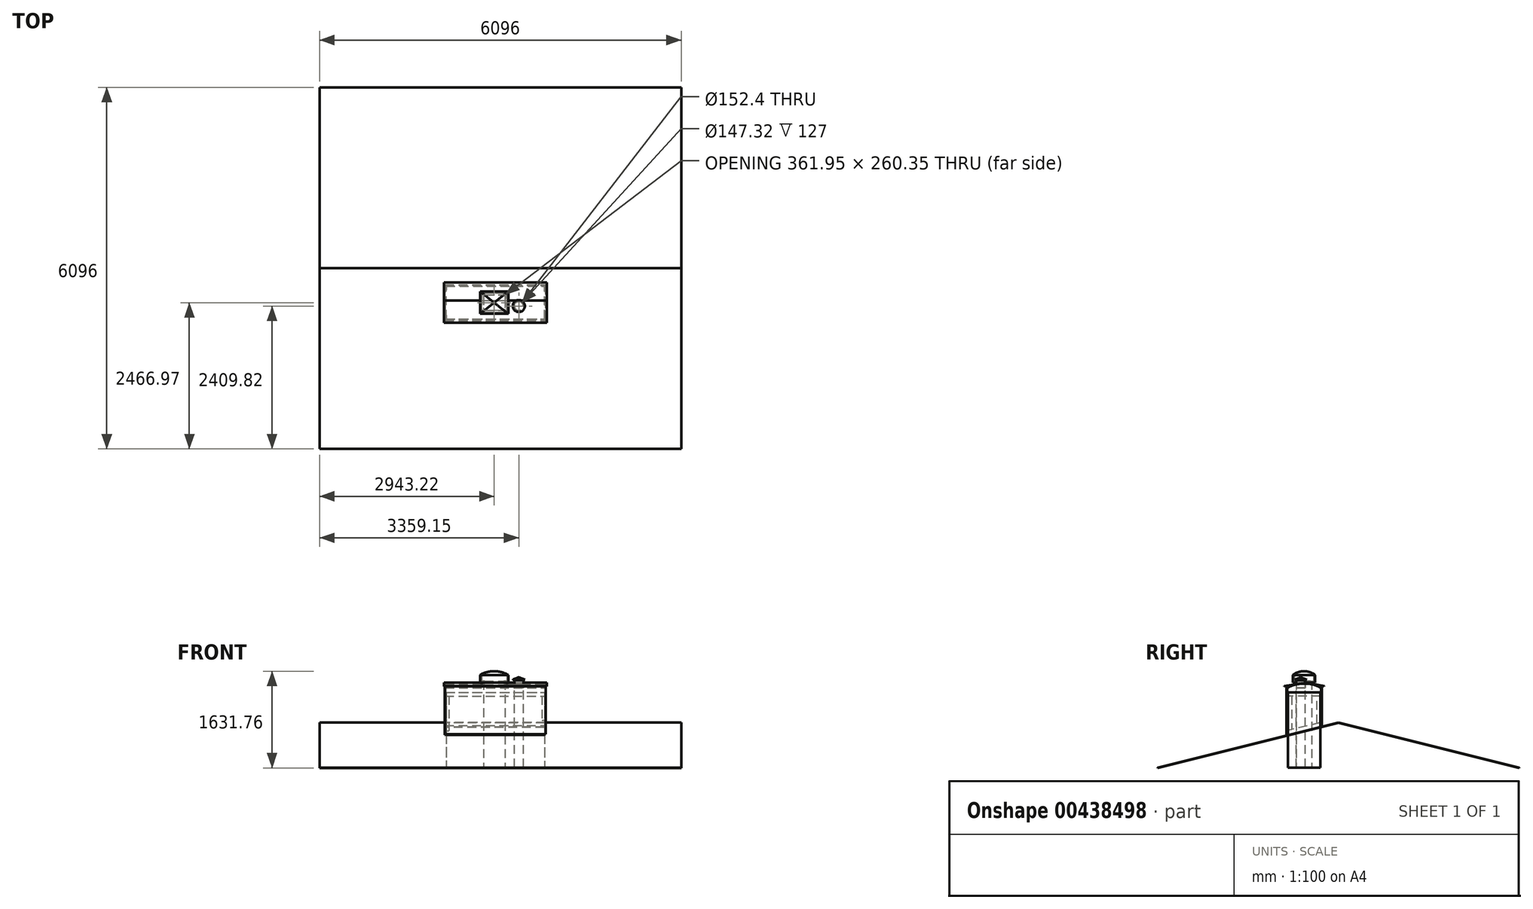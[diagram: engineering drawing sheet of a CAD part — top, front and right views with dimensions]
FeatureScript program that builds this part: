
annotation { "Feature Type Name" : "Feature", "Feature Type Description" : "" }
export const myFeature = defineFeature(function(context is Context, id is Id, definition is map)
    precondition{}
    {
        {
            var Q0;
            Q0=qCreatedBy(makeId("Right.planeOp"),FACE);
            var sketch = newSketch(context, id + "F0", { "sketchPlane" : qUnion([Q0])});
            skLineSegment(sketch, "E0", {"start": v(-3048, 0) * mm, "end": v(0, 762) * mm});
            skLineSegment(sketch, "E1", {"start": v(0, 762) * mm, "end": v(0, -40.65) * mm, "construction": true});
            skLineSegment(sketch, "E2.MirrorCS", {"start": v(3048, 0) * mm, "end": v(0, 762) * mm});
            skLineSegment(sketch, "E3.0", {"start": v(3046.46, -6.16) * mm, "end": v(0, 755.45) * mm});
            skLineSegment(sketch, "E3.1", {"start": v(-3046.46, -6.16) * mm, "end": v(0, 755.45) * mm});
            skLineSegment(sketch, "E4", {"start": v(-3048, 0) * mm, "end": v(-3046.46, -6.16) * mm});
            skLineSegment(sketch, "E5", {"start": v(3048, 0) * mm, "end": v(3046.46, -6.16) * mm});
            skSolve(sketch);
        }
        {
            var Q0;
            Q0=makeQuery(id+"F0.imprint","IMPRINT",FACE,{"disambiguationData":[TD([[makeQuery(id+"F0.imprint","IMPRINT",EDGE,{"derivedFrom":sQuery(id+"F0.wireOp",EDGE,"E0")}),-1.0]])]});
            var Q1;
            Q1=sQuery(id+"F0.wireOp",EDGE,"E0");
            var Q2;
            Q2=sQuery(id+"F0.wireOp",EDGE,"E2.MirrorCS");
            extrude(context, id + "F1", {"entities" : qUnion([Q0]), "surfaceEntities" : qUnion([Q1, Q2]), "depth" : 3048 * mm, "hasSecondDirection" : true, "secondDirectionOppositeDirection" : true, "secondDirectionDepth" : 3048 * mm, "offsetDistance" : 25.4 * mm});
        }
        {
            var Q0;
            Q0=qCreatedBy(makeId("Top.planeOp"),FACE);
            var sketch = newSketch(context, id + "F2", { "sketchPlane" : qUnion([Q0])});
            skLineSegment(sketch, "E6.bottom", {"start": v(-914.4, -854.07) * mm, "end": v(742.95, -854.07) * mm});
            skLineSegment(sketch, "E6.top", {"start": v(-914.4, -304.8) * mm, "end": v(742.95, -304.8) * mm});
            skLineSegment(sketch, "E6.left", {"start": v(-914.4, -854.07) * mm, "end": v(-914.4, -304.8) * mm});
            skLineSegment(sketch, "E6.right", {"start": v(742.95, -854.07) * mm, "end": v(742.95, -304.8) * mm});
            skSolve(sketch);
        }
        {
            var Q0;
            Q0=makeQuery(id+"F2.imprint","IMPRINT",FACE,{"disambiguationData":[TD([[makeQuery(id+"F2.imprint","IMPRINT",EDGE,{"derivedFrom":sQuery(id+"F2.wireOp",EDGE,"E6.bottom")}),1.0]])]});
            extrude(context, id + "F3", {"entities" : qUnion([Q0]), "operationType" : NewBodyOperationType.REMOVE, "endBound" : BoundingType.THROUGH_ALL, "depth" : 25.4 * mm, "offsetDistance" : 25.4 * mm});
        }
        {
            var Q0;
            Q0 = qSketchRegion(id + "F2", true);
            extrude(context, id + "F4", {"entities" : qUnion([Q0]), "depth" : 1270 * mm, "offsetDistance" : 25.4 * mm});
        }
        {
            var Q0;
            Q0=makeQuery(id+"F4.opExtrude","CAP_FACE",FACE,{"disambiguationData":[OSD([sQuery(id+"F2.wireOp",EDGE,"E6.bottom"),sQuery(id+"F2.wireOp",EDGE,"E6.top"),sQuery(id+"F2.wireOp",EDGE,"E6.left"),sQuery(id+"F2.wireOp",EDGE,"E6.right")])],"isStart":false});
            var sketch = newSketch(context, id + "F5", { "sketchPlane" : qUnion([Q0])});
            skLineSegment(sketch, "E7.bottom", {"start": v(-927.1, -866.77) * mm, "end": v(755.65, -866.77) * mm});
            skLineSegment(sketch, "E7.top", {"start": v(-927.1, -292.1) * mm, "end": v(755.65, -292.1) * mm});
            skLineSegment(sketch, "E7.left", {"start": v(-927.1, -866.77) * mm, "end": v(-927.1, -292.1) * mm});
            skLineSegment(sketch, "E7.right", {"start": v(755.65, -866.77) * mm, "end": v(755.65, -292.1) * mm});
            skSolve(sketch);
        }
        {
            var Q0;
            Q0 = qSketchRegion(id + "F5", true);
            extrude(context, id + "F6", {"entities" : qUnion([Q0]), "operationType" : NewBodyOperationType.ADD, "depth" : 76.2 * mm, "offsetDistance" : 25.4 * mm});
        }
        {
            var Q0;
            Q0=makeQuery(id+"F6.opExtrude","CAP_FACE",FACE,{"disambiguationData":[OSD([sQuery(id+"F5.wireOp",EDGE,"E7.bottom"),sQuery(id+"F5.wireOp",EDGE,"E7.top"),sQuery(id+"F5.wireOp",EDGE,"E7.left"),sQuery(id+"F5.wireOp",EDGE,"E7.right")])],"isStart":false});
            var sketch = newSketch(context, id + "F7", { "sketchPlane" : qUnion([Q0])});
            skLineSegment(sketch, "E8.bottom", {"start": v(-266.7, -419.1) * mm, "end": v(57.15, -419.1) * mm});
            skLineSegment(sketch, "E8.top", {"start": v(-266.7, -742.95) * mm, "end": v(57.15, -742.95) * mm});
            skLineSegment(sketch, "E8.left", {"start": v(-317.5, -469.9) * mm, "end": v(-317.5, -692.15) * mm});
            skLineSegment(sketch, "E8.right", {"start": v(107.95, -469.9) * mm, "end": v(107.95, -692.15) * mm});
            skPoint(sketch, "E9.visualSharp", {"position": v(-317.5, -419.1) * mm});
            skArc(sketch, "E9.filletArc", {"start": v(-266.7, -419.1) * mm, "mid": v(-302.62, -433.98) * mm, "end": v(-317.5, -469.9) * mm});
            skPoint(sketch, "E10.visualSharp", {"position": v(107.95, -419.1) * mm});
            skArc(sketch, "E10.filletArc", {"start": v(107.95, -469.9) * mm, "mid": v(93.07, -433.98) * mm, "end": v(57.15, -419.1) * mm});
            skPoint(sketch, "E11.visualSharp", {"position": v(107.95, -742.95) * mm});
            skArc(sketch, "E11.filletArc", {"start": v(57.15, -742.95) * mm, "mid": v(93.07, -728.07) * mm, "end": v(107.95, -692.15) * mm});
            skPoint(sketch, "E12.visualSharp", {"position": v(-317.5, -742.95) * mm});
            skArc(sketch, "E12.filletArc", {"start": v(-317.5, -692.15) * mm, "mid": v(-302.62, -728.07) * mm, "end": v(-266.7, -742.95) * mm});
            skCircle(sketch, "E13", {"center": v(311.15, -638.17) * mm, "radius": 76.2 * mm});
            skArc(sketch, "E14.0", {"start": v(-266.7, -450.85) * mm, "mid": v(-280.17, -456.43) * mm, "end": v(-285.75, -469.9) * mm});
            skLineSegment(sketch, "E14.1", {"start": v(-285.75, -469.9) * mm, "end": v(-285.75, -692.15) * mm});
            skLineSegment(sketch, "E14.2", {"start": v(-266.7, -450.85) * mm, "end": v(57.15, -450.85) * mm});
            skArc(sketch, "E14.3", {"start": v(-285.75, -692.15) * mm, "mid": v(-280.17, -705.62) * mm, "end": v(-266.7, -711.2) * mm});
            skArc(sketch, "E14.4", {"start": v(76.2, -469.9) * mm, "mid": v(70.62, -456.43) * mm, "end": v(57.15, -450.85) * mm});
            skLineSegment(sketch, "E14.5", {"start": v(76.2, -469.9) * mm, "end": v(76.2, -692.15) * mm});
            skArc(sketch, "E14.6", {"start": v(57.15, -711.2) * mm, "mid": v(70.62, -705.62) * mm, "end": v(76.2, -692.15) * mm});
            skLineSegment(sketch, "E14.7", {"start": v(-266.7, -711.2) * mm, "end": v(57.15, -711.2) * mm});
            skLineSegment(sketch, "E15.0", {"start": v(749.3, -298.45) * mm, "end": v(-920.75, -298.45) * mm});
            skLineSegment(sketch, "E15.1", {"start": v(749.3, -860.42) * mm, "end": v(749.3, -298.45) * mm});
            skLineSegment(sketch, "E15.2", {"start": v(-920.75, -860.42) * mm, "end": v(749.3, -860.42) * mm});
            skLineSegment(sketch, "E15.3", {"start": v(-920.75, -298.45) * mm, "end": v(-920.75, -860.42) * mm});
            skCircle(sketch, "E16.0", {"center": v(311.15, -638.17) * mm, "radius": 73.66 * mm});
            skSolve(sketch);
        }
        {
            var Q0;
            Q0=makeQuery(id+"F7.imprint","IMPRINT",FACE,{"disambiguationData":[TD([[makeQuery(id+"F7.imprint","IMPRINT",EDGE,{"derivedFrom":sQuery(id+"F7.wireOp",EDGE,"E8.bottom")}),-1.0]])]});
            extrude(context, id + "F8", {"entities" : qUnion([Q0]), "operationType" : NewBodyOperationType.ADD, "depth" : 114.3 * mm, "offsetDistance" : 25.4 * mm});
        }
        {
            var Q0;
            Q0=makeQuery(id+"F7.imprint","IMPRINT",FACE,{"disambiguationData":[TD([[makeQuery(id+"F7.imprint","IMPRINT",EDGE,{"derivedFrom":sQuery(id+"F7.wireOp",EDGE,"E13")}),1.0]])]});
            var Q1;
            Q1=makeQuery(id+"F7.imprint","IMPRINT",FACE,{"disambiguationData":[TD([[makeQuery(id+"F7.imprint","IMPRINT",EDGE,{"derivedFrom":sQuery(id+"F7.wireOp",EDGE,"E16.0")}),1.0]])]});
            extrude(context, id + "F9", {"entities" : qUnion([Q0, Q1]), "operationType" : NewBodyOperationType.REMOVE, "endBound" : BoundingType.THROUGH_ALL, "oppositeDirection" : true, "depth" : 25.4 * mm, "offsetDistance" : 25.4 * mm, "hasSecondDirection" : true, "secondDirectionBound" : SecondDirectionBoundingType.THROUGH_ALL, "secondDirectionOppositeDirection" : false, "secondDirectionDepth" : 25.4 * mm});
        }
        {
            var Q0;
            Q0=makeQuery(id+"F6.opExtrude","SWEPT_FACE",FACE,{"disambiguationData":[OSD([sQuery(id+"F5.wireOp",EDGE,"E7.right")])]});
            var sketch = newSketch(context, id + "F10", { "sketchPlane" : qUnion([Q0])});
            skArc(sketch, "E17", {"start": v(-292.1, 1346.2) * mm, "mid": v(-579.44, 1416.05) * mm, "end": v(-866.77, 1346.2) * mm});
            skLineSegment(sketch, "E18", {"start": v(-866.77, 1346.2) * mm, "end": v(-292.1, 1346.2) * mm});
            skSolve(sketch);
        }
        {
            var Q0;
            Q0=makeQuery(id+"F10.imprint","IMPRINT",FACE,{"disambiguationData":[TD([[makeQuery(id+"F10.imprint","IMPRINT",EDGE,{"derivedFrom":sQuery(id+"F10.wireOp",EDGE,"E17")}),1.0]])]});
            var Q1;
            Q1=makeQuery(id+"F6.opExtrude","SWEPT_FACE",FACE,{"disambiguationData":[OSD([sQuery(id+"F5.wireOp",EDGE,"E7.left")])]});
            extrude(context, id + "F11", {"entities" : qUnion([Q0]), "operationType" : NewBodyOperationType.ADD, "endBound" : BoundingType.UP_TO_SURFACE, "oppositeDirection" : true, "depth" : 25.4 * mm, "endBoundEntityFace" : qUnion([Q1]), "offsetDistance" : 25.4 * mm});
        }
        {
            var Q0;
            Q0=makeQuery(id+"F7.imprint","IMPRINT",FACE,{"disambiguationData":[TD([[makeQuery(id+"F7.imprint","IMPRINT",EDGE,{"derivedFrom":sQuery(id+"F7.wireOp",EDGE,"E13")}),1.0]])]});
            var Q1;
            Q1=makeQuery(id+"F7.imprint","IMPRINT",FACE,{"disambiguationData":[TD([[makeQuery(id+"F7.imprint","IMPRINT",EDGE,{"derivedFrom":sQuery(id+"F7.wireOp",EDGE,"E16.0")}),1.0]])]});
            extrude(context, id + "F12", {"entities" : qUnion([Q0, Q1]), "operationType" : NewBodyOperationType.REMOVE, "endBound" : BoundingType.THROUGH_ALL, "depth" : 25.4 * mm, "offsetDistance" : 25.4 * mm});
        }
        {
            var Q0;
            Q0=makeQuery(id+"F8.opExtrude","CAP_FACE",FACE,{"disambiguationData":[OSD([sQuery(id+"F7.wireOp",EDGE,"E8.bottom"),sQuery(id+"F7.wireOp",EDGE,"E8.top"),sQuery(id+"F7.wireOp",EDGE,"E8.left"),sQuery(id+"F7.wireOp",EDGE,"E8.right"),sQuery(id+"F7.wireOp",EDGE,"E9.filletArc"),sQuery(id+"F7.wireOp",EDGE,"E10.filletArc"),sQuery(id+"F7.wireOp",EDGE,"E11.filletArc"),sQuery(id+"F7.wireOp",EDGE,"E12.filletArc"),sQuery(id+"F7.wireOp",EDGE,"E14.0"),sQuery(id+"F7.wireOp",EDGE,"E14.1"),sQuery(id+"F7.wireOp",EDGE,"E14.2"),sQuery(id+"F7.wireOp",EDGE,"E14.3"),sQuery(id+"F7.wireOp",EDGE,"E14.4"),sQuery(id+"F7.wireOp",EDGE,"E14.5"),sQuery(id+"F7.wireOp",EDGE,"E14.6"),sQuery(id+"F7.wireOp",EDGE,"E14.7")])],"isStart":false});
            var sketch = newSketch(context, id + "F13", { "sketchPlane" : qUnion([Q0])});
            skLineSegment(sketch, "E19.0", {"start": v(-266.7, -450.85) * mm, "end": v(57.15, -450.85) * mm});
            skArc(sketch, "E20.0", {"start": v(76.2, -469.9) * mm, "mid": v(70.62, -456.43) * mm, "end": v(57.15, -450.85) * mm});
            skLineSegment(sketch, "E21.0", {"start": v(76.2, -469.9) * mm, "end": v(76.2, -692.15) * mm});
            skArc(sketch, "E22.0", {"start": v(57.15, -711.2) * mm, "mid": v(70.62, -705.62) * mm, "end": v(76.2, -692.15) * mm});
            skLineSegment(sketch, "E23.0", {"start": v(-266.7, -711.2) * mm, "end": v(57.15, -711.2) * mm});
            skArc(sketch, "E24.0", {"start": v(-285.75, -692.15) * mm, "mid": v(-280.17, -705.62) * mm, "end": v(-266.7, -711.2) * mm});
            skLineSegment(sketch, "E25.0", {"start": v(-285.75, -469.9) * mm, "end": v(-285.75, -692.15) * mm});
            skArc(sketch, "E26.0", {"start": v(-266.7, -450.85) * mm, "mid": v(-280.17, -456.43) * mm, "end": v(-285.75, -469.9) * mm});
            skSolve(sketch);
        }
        {
            var Q0;
            Q0=makeQuery(id+"F13.imprint","IMPRINT",FACE,{"disambiguationData":[TD([[makeQuery(id+"F13.imprint","IMPRINT",EDGE,{"derivedFrom":sQuery(id+"F13.wireOp",EDGE,"E19.0")}),-1.0]])]});
            extrude(context, id + "F14", {"entities" : qUnion([Q0]), "operationType" : NewBodyOperationType.REMOVE, "endBound" : BoundingType.THROUGH_ALL, "oppositeDirection" : true, "depth" : 25.4 * mm, "offsetDistance" : 25.4 * mm});
        }
        {
            var Q0;
            Q0=makeQuery(id+"F8.opExtrude","CAP_FACE",FACE,{"disambiguationData":[OSD([sQuery(id+"F7.wireOp",EDGE,"E8.bottom"),sQuery(id+"F7.wireOp",EDGE,"E8.top"),sQuery(id+"F7.wireOp",EDGE,"E8.left"),sQuery(id+"F7.wireOp",EDGE,"E8.right"),sQuery(id+"F7.wireOp",EDGE,"E9.filletArc"),sQuery(id+"F7.wireOp",EDGE,"E10.filletArc"),sQuery(id+"F7.wireOp",EDGE,"E11.filletArc"),sQuery(id+"F7.wireOp",EDGE,"E12.filletArc"),sQuery(id+"F7.wireOp",EDGE,"E14.0"),sQuery(id+"F7.wireOp",EDGE,"E14.1"),sQuery(id+"F7.wireOp",EDGE,"E14.2"),sQuery(id+"F7.wireOp",EDGE,"E14.3"),sQuery(id+"F7.wireOp",EDGE,"E14.4"),sQuery(id+"F7.wireOp",EDGE,"E14.5"),sQuery(id+"F7.wireOp",EDGE,"E14.6"),sQuery(id+"F7.wireOp",EDGE,"E14.7")])],"isStart":false});
            var sketch = newSketch(context, id + "F15", { "sketchPlane" : qUnion([Q0])});
            skLineSegment(sketch, "E27.bottom", {"start": v(-342.9, -768.35) * mm, "end": v(133.35, -768.35) * mm});
            skLineSegment(sketch, "E27.top", {"start": v(-342.9, -393.7) * mm, "end": v(133.35, -393.7) * mm});
            skLineSegment(sketch, "E27.left", {"start": v(-342.9, -768.35) * mm, "end": v(-342.9, -393.7) * mm});
            skLineSegment(sketch, "E27.right", {"start": v(133.35, -768.35) * mm, "end": v(133.35, -393.7) * mm});
            skLineSegment(sketch, "E28.0", {"start": v(-317.5, -742.95) * mm, "end": v(-317.5, -419.1) * mm});
            skLineSegment(sketch, "E28.1", {"start": v(-317.5, -742.95) * mm, "end": v(107.95, -742.95) * mm});
            skLineSegment(sketch, "E28.2", {"start": v(107.95, -742.95) * mm, "end": v(107.95, -419.1) * mm});
            skLineSegment(sketch, "E28.3", {"start": v(-317.5, -419.1) * mm, "end": v(107.95, -419.1) * mm});
            skSolve(sketch);
        }
        {
            var Q0;
            Q0=makeQuery(id+"F15.imprint","IMPRINT",FACE,{"disambiguationData":[TD([[makeQuery(id+"F15.imprint","IMPRINT",EDGE,{"derivedFrom":sQuery(id+"F15.wireOp",EDGE,"E27.bottom")}),1.0]])]});
            extrude(context, id + "F16", {"entities" : qUnion([Q0]), "depth" : 101.6 * mm, "offsetDistance" : 25.4 * mm, "hasSecondDirection" : true, "secondDirectionOppositeDirection" : true, "secondDirectionDepth" : 25.4 * mm});
        }
        {
            var Q0;
            Q0=makeQuery(id+"F16.opExtrude","SWEPT_FACE",FACE,{"disambiguationData":[OSD([sQuery(id+"F15.wireOp",EDGE,"E27.bottom")])]});
            var sketch = newSketch(context, id + "F17", { "sketchPlane" : qUnion([Q0])});
            skArc(sketch, "E29", {"start": v(133.35, 1562.1) * mm, "mid": v(-104.77, 1625.6) * mm, "end": v(-342.9, 1562.1) * mm});
            skSolve(sketch);
        }
        {
            var Q0;
            Q0=makeQuery(id+"F16.opExtrude","SWEPT_FACE",FACE,{"disambiguationData":[OSD([sQuery(id+"F15.wireOp",EDGE,"E27.right")])]});
            var sketch = newSketch(context, id + "F18", { "sketchPlane" : qUnion([Q0])});
            skArc(sketch, "E30", {"start": v(-393.7, 1562.1) * mm, "mid": v(-581.02, 1625.6) * mm, "end": v(-768.35, 1562.1) * mm});
            skLineSegment(sketch, "E31.top", {"start": v(-768.35, 1738.66) * mm, "end": v(-393.7, 1738.66) * mm});
            skLineSegment(sketch, "E31.left", {"start": v(-768.35, 1562.1) * mm, "end": v(-768.35, 1738.66) * mm});
            skLineSegment(sketch, "E31.right", {"start": v(-393.7, 1562.1) * mm, "end": v(-393.7, 1738.66) * mm});
            skSolve(sketch);
        }
        {
            var Q0;
            Q0=makeQuery(id+"F17.imprint","IMPRINT",FACE,{"disambiguationData":[TD([[makeQuery(id+"F17.imprint","IMPRINT",EDGE,{"derivedFrom":sQuery(id+"F17.wireOp",EDGE,"E29")}),1.0]])]});
            var Q1;
            Q1=makeQuery(id+"F16.opExtrude","SWEPT_FACE",FACE,{"disambiguationData":[OSD([sQuery(id+"F15.wireOp",EDGE,"E27.top")])]});
            extrude(context, id + "F19", {"entities" : qUnion([Q0]), "operationType" : NewBodyOperationType.ADD, "endBound" : BoundingType.UP_TO_SURFACE, "oppositeDirection" : true, "depth" : 25.4 * mm, "endBoundEntityFace" : qUnion([Q1]), "offsetDistance" : 25.4 * mm});
        }
        {
            var Q0;
            Q0=makeQuery(id+"F18.imprint","IMPRINT",FACE,{"disambiguationData":[TD([[makeQuery(id+"F18.imprint","IMPRINT",EDGE,{"derivedFrom":sQuery(id+"F18.wireOp",EDGE,"E30")}),-1.0]])]});
            extrude(context, id + "F20", {"entities" : qUnion([Q0]), "operationType" : NewBodyOperationType.REMOVE, "endBound" : BoundingType.THROUGH_ALL, "oppositeDirection" : true, "depth" : 25.4 * mm, "offsetDistance" : 25.4 * mm});
        }
        {
            var Q0;
            Q0=makeQuery(id+"F7.imprint","IMPRINT",FACE,{"disambiguationData":[TD([[makeQuery(id+"F7.imprint","IMPRINT",EDGE,{"derivedFrom":sQuery(id+"F7.wireOp",EDGE,"E13")}),1.0]])]});
            extrude(context, id + "F21", {"entities" : qUnion([Q0]), "depth" : 127 * mm, "offsetDistance" : 25.4 * mm});
        }
        {
            var Q0;
            Q0=makeQuery(id+"F21.opExtrude","SWEPT_FACE",FACE,{"disambiguationData":[OSD([sQuery(id+"F7.wireOp",EDGE,"E13")])]});
            cPlane(context, id + "F22", {"entities" : qUnion([Q0]), "cplaneType" : CPlaneType.LINE_ANGLE, "offset" : 25.4 * mm, "angle" : 0 * degree, "width" : 152.4 * mm, "height" : 152.4 * mm});
        }
        {
            var Q0;
            Q0=qCreatedBy(id+"F22.planeOp",FACE);
            var sketch = newSketch(context, id + "F23", { "sketchPlane" : qUnion([Q0])});
            skLineSegment(sketch, "E32", {"start": v(638.17, 1430.23) * mm, "end": v(638.17, 1564.53) * mm, "construction": true});
            skLineSegment(sketch, "E33", {"start": v(638.17, 1521.29) * mm, "end": v(537.47, 1483.52) * mm});
            skLineSegment(sketch, "E34", {"start": v(537.47, 1483.52) * mm, "end": v(536.57, 1485.9) * mm});
            skLineSegment(sketch, "E35", {"start": v(536.57, 1485.9) * mm, "end": v(638.17, 1524) * mm});
            skLineSegment(sketch, "E36", {"start": v(638.17, 1524) * mm, "end": v(638.17, 1521.29) * mm});
            skSolve(sketch);
        }
        {
            var Q0;
            Q0=makeQuery(id+"F23.imprint","IMPRINT",FACE,{"disambiguationData":[TD([[makeQuery(id+"F23.imprint","IMPRINT",EDGE,{"derivedFrom":sQuery(id+"F23.wireOp",EDGE,"E33")}),-1.0]])]});
            var Q1;
            Q1=sQuery(id+"F23.wireOp",EDGE,"E32");
            revolve(context, id + "F24", {"operationType" : NewBodyOperationType.ADD, "entities" : qUnion([Q0]), "axis" : qUnion([Q1]), "revolveType" : RevolveType.FULL});
        }
        {
            var Q0;
            Q0=makeQuery(id+"F4.opExtrude","SWEPT_FACE",FACE,{"disambiguationData":[OSD([sQuery(id+"F2.wireOp",EDGE,"E6.bottom")])]});
            var sketch = newSketch(context, id + "F25", { "sketchPlane" : qUnion([Q0])});
            skLineSegment(sketch, "E37.bottom", {"start": v(-933.45, 1270) * mm, "end": v(762, 1270) * mm});
            skLineSegment(sketch, "E37.top", {"start": v(-933.45, 1206.5) * mm, "end": v(762, 1206.5) * mm});
            skLineSegment(sketch, "E37.left", {"start": v(-933.45, 1270) * mm, "end": v(-933.45, 1206.5) * mm});
            skLineSegment(sketch, "E37.right", {"start": v(762, 1270) * mm, "end": v(762, 1206.5) * mm});
            skLineSegment(sketch, "E38.bottom", {"start": v(-933.45, 622.3) * mm, "end": v(762, 622.3) * mm});
            skLineSegment(sketch, "E38.top", {"start": v(-933.45, 558.8) * mm, "end": v(762, 558.8) * mm});
            skLineSegment(sketch, "E38.left", {"start": v(-933.45, 622.3) * mm, "end": v(-933.45, 558.8) * mm});
            skLineSegment(sketch, "E38.right", {"start": v(762, 622.3) * mm, "end": v(762, 558.8) * mm});
            skLineSegment(sketch, "E39.bottom", {"start": v(-933.45, 1206.5) * mm, "end": v(-869.95, 1206.5) * mm});
            skLineSegment(sketch, "E39.top", {"start": v(-933.45, 622.3) * mm, "end": v(-869.95, 622.3) * mm});
            skLineSegment(sketch, "E39.left", {"start": v(-933.45, 1206.5) * mm, "end": v(-933.45, 622.3) * mm});
            skLineSegment(sketch, "E39.right", {"start": v(-869.95, 1206.5) * mm, "end": v(-869.95, 622.3) * mm});
            skLineSegment(sketch, "E40.bottom", {"start": v(762, 1206.5) * mm, "end": v(698.5, 1206.5) * mm});
            skLineSegment(sketch, "E40.top", {"start": v(762, 622.3) * mm, "end": v(698.5, 622.3) * mm});
            skLineSegment(sketch, "E40.left", {"start": v(762, 1206.5) * mm, "end": v(762, 622.3) * mm});
            skLineSegment(sketch, "E40.right", {"start": v(698.5, 1206.5) * mm, "end": v(698.5, 622.3) * mm});
            skSolve(sketch);
        }
        {
            var Q0;
            {var subQ1=sQuery(id+"F25.wireOp",EDGE,"E37.top");Q0=makeQuery(id+"F25.imprint","IMPRINT",FACE,{"disambiguationData":[TD([[makeQuery(id+"F25.imprint","IMPRINT",EDGE,{"derivedFrom":subQ1}),1.0]])]});}
            var Q1;
            {var subQ3=sQuery(id+"F25.wireOp",EDGE,"E37.left");Q1=makeQuery(id+"F25.imprint","IMPRINT",FACE,{"disambiguationData":[TD([[makeQuery(id+"F25.imprint","IMPRINT",EDGE,{"derivedFrom":subQ3}),1.0]])]});}
            var Q2;
            {var subQ3=sQuery(id+"F25.wireOp",EDGE,"E37.right");Q2=makeQuery(id+"F25.imprint","IMPRINT",FACE,{"disambiguationData":[TD([[makeQuery(id+"F25.imprint","IMPRINT",EDGE,{"derivedFrom":subQ3}),-1.0]])]});}
            extrude(context, id + "F26", {"entities" : qUnion([Q0, Q1, Q2]), "depth" : 19.05 * mm, "offsetDistance" : 25.4 * mm});
        }
        {
            var Q0;
            {var subQ0=sQuery(id+"F25.wireOp",EDGE,"E39.right");Q0=makeQuery(id+"F25.imprint","IMPRINT",FACE,{"disambiguationData":[TD([[makeQuery(id+"F25.imprint","IMPRINT",EDGE,{"derivedFrom":subQ0}),-1.0]])]});}
            var Q1;
            {var subQ0=sQuery(id+"F25.wireOp",EDGE,"E39.left");Q1=makeQuery(id+"F25.imprint","IMPRINT",FACE,{"disambiguationData":[TD([[makeQuery(id+"F25.imprint","IMPRINT",EDGE,{"derivedFrom":subQ0}),1.0]])]});}
            extrude(context, id + "F27", {"entities" : qUnion([Q0, Q1]), "depth" : 19.05 * mm, "offsetDistance" : 25.4 * mm});
        }
        {
            var Q0;
            Q0=makeQuery(id+"F4.opExtrude","SWEPT_FACE",FACE,{"disambiguationData":[OSD([sQuery(id+"F2.wireOp",EDGE,"E6.left")])]});
            var sketch = newSketch(context, id + "F28", { "sketchPlane" : qUnion([Q0])});
            skLineSegment(sketch, "E41.bottom", {"start": v(301.62, 1270) * mm, "end": v(854.07, 1270) * mm});
            skLineSegment(sketch, "E41.top", {"start": v(301.62, 1206.5) * mm, "end": v(854.07, 1206.5) * mm});
            skLineSegment(sketch, "E41.left", {"start": v(301.62, 1270) * mm, "end": v(301.62, 1206.5) * mm});
            skLineSegment(sketch, "E41.right", {"start": v(854.07, 1270) * mm, "end": v(854.07, 1206.5) * mm});
            skLineSegment(sketch, "E42", {"start": v(854.07, 558.8) * mm, "end": v(301.62, 693.33) * mm});
            skLineSegment(sketch, "E43", {"start": v(301.62, 693.33) * mm, "end": v(301.62, 758.69) * mm});
            skLineSegment(sketch, "E44", {"start": v(301.62, 758.69) * mm, "end": v(854.07, 624.16) * mm});
            skLineSegment(sketch, "E45", {"start": v(854.07, 624.16) * mm, "end": v(854.07, 558.8) * mm});
            skLineSegment(sketch, "E46", {"start": v(301.62, 1206.5) * mm, "end": v(301.62, 758.69) * mm});
            skLineSegment(sketch, "E47", {"start": v(365.12, 743.22) * mm, "end": v(365.12, 1206.5) * mm});
            skLineSegment(sketch, "E48", {"start": v(854.07, 1206.5) * mm, "end": v(854.07, 624.16) * mm});
            skLineSegment(sketch, "E49", {"start": v(790.57, 1206.5) * mm, "end": v(790.57, 639.62) * mm});
            skSolve(sketch);
        }
        {
            var Q0;
            {var subQ5=sQuery(id+"F28.wireOp",EDGE,"E41.right");Q0=makeQuery(id+"F28.imprint","IMPRINT",FACE,{"disambiguationData":[TD([[makeQuery(id+"F28.imprint","IMPRINT",EDGE,{"derivedFrom":subQ5}),-1.0]])]});}
            var Q1;
            {var subQ3=sQuery(id+"F28.wireOp",EDGE,"E41.left");Q1=makeQuery(id+"F28.imprint","IMPRINT",FACE,{"disambiguationData":[TD([[makeQuery(id+"F28.imprint","IMPRINT",EDGE,{"derivedFrom":subQ3}),1.0]])]});}
            extrude(context, id + "F29", {"entities" : qUnion([Q0, Q1]), "depth" : 19.05 * mm, "offsetDistance" : 25.4 * mm});
        }
        {
            var Q0;
            {var subQ0=sQuery(id+"F28.wireOp",EDGE,"E47");Q0=makeQuery(id+"F28.imprint","IMPRINT",FACE,{"disambiguationData":[TD([[makeQuery(id+"F28.imprint","IMPRINT",EDGE,{"derivedFrom":subQ0}),1.0]])]});}
            var Q1;
            {var subQ0=sQuery(id+"F28.wireOp",EDGE,"E46");Q1=makeQuery(id+"F28.imprint","IMPRINT",FACE,{"disambiguationData":[TD([[makeQuery(id+"F28.imprint","IMPRINT",EDGE,{"derivedFrom":subQ0}),1.0]])]});}
            extrude(context, id + "F30", {"entities" : qUnion([Q0, Q1]), "depth" : 19.05 * mm, "offsetDistance" : 25.4 * mm});
        }
        {
            var Q0;
            {var subQ0=sQuery(id+"F28.wireOp",EDGE,"E48");Q0=makeQuery(id+"F28.imprint","IMPRINT",FACE,{"disambiguationData":[TD([[makeQuery(id+"F28.imprint","IMPRINT",EDGE,{"derivedFrom":subQ0}),-1.0]])]});}
            extrude(context, id + "F31", {"entities" : qUnion([Q0]), "depth" : 19.05 * mm, "offsetDistance" : 25.4 * mm});
        }
        {
            var Q0;
            {var subQ0=sQuery(id+"F28.wireOp",EDGE,"E45");Q0=makeQuery(id+"F28.imprint","IMPRINT",FACE,{"disambiguationData":[TD([[makeQuery(id+"F28.imprint","IMPRINT",EDGE,{"derivedFrom":subQ0}),-1.0]])]});}
            var Q1;
            {var subQ0=sQuery(id+"F28.wireOp",EDGE,"E43");Q1=makeQuery(id+"F28.imprint","IMPRINT",FACE,{"disambiguationData":[TD([[makeQuery(id+"F28.imprint","IMPRINT",EDGE,{"derivedFrom":subQ0}),-1.0]])]});}
            extrude(context, id + "F32", {"entities" : qUnion([Q0, Q1]), "depth" : 19.05 * mm, "offsetDistance" : 25.4 * mm});
        }
        {
            var Q0;
            Q0=makeQuery(id+"F4.opExtrude","SWEPT_FACE",FACE,{"disambiguationData":[OSD([sQuery(id+"F2.wireOp",EDGE,"E6.top")])]});
            var sketch = newSketch(context, id + "F33", { "sketchPlane" : qUnion([Q0])});
            skLineSegment(sketch, "E50.bottom", {"start": v(-698.5, 1206.5) * mm, "end": v(-762, 1206.5) * mm});
            skLineSegment(sketch, "E50.top", {"start": v(-698.5, 800.1) * mm, "end": v(-762, 800.1) * mm});
            skLineSegment(sketch, "E50.left", {"start": v(-698.5, 1206.5) * mm, "end": v(-698.5, 800.1) * mm});
            skLineSegment(sketch, "E50.right", {"start": v(-762, 1206.5) * mm, "end": v(-762, 800.1) * mm});
            skSolve(sketch);
        }
        {
            var Q0;
            {var subQ0=sQuery(id+"F33.wireOp",EDGE,"E50.left");Q0=makeQuery(id+"F33.imprint","IMPRINT",FACE,{"disambiguationData":[TD([[makeQuery(id+"F33.imprint","IMPRINT",EDGE,{"derivedFrom":subQ0}),-1.0]])]});}
            var Q1;
            {var subQ0=sQuery(id+"F33.wireOp",EDGE,"E50.right");Q1=makeQuery(id+"F33.imprint","IMPRINT",FACE,{"disambiguationData":[TD([[makeQuery(id+"F33.imprint","IMPRINT",EDGE,{"derivedFrom":subQ0}),1.0]])]});}
            extrude(context, id + "F34", {"entities" : qUnion([Q0, Q1]), "operationType" : NewBodyOperationType.ADD, "depth" : 19.05 * mm, "offsetDistance" : 25.4 * mm});
        }
        {
            var Q0;
            {var subQ0=sQuery(id+"F5.wireOp",EDGE,"E7.left");Q0=makeQuery(id+"F11.boolean.opBoolean","MERGE",FACE,{"derivedFrom":[makeQuery(id+"F6.opExtrude","SWEPT_FACE",FACE,{"disambiguationData":[OSD([subQ0])]}),makeQuery(id+"F11.opExtrude","CAP_FACE",FACE,{"disambiguationData":[OSD([subQ0])],"isStart":false})]});}
            var sketch = newSketch(context, id + "F35", { "sketchPlane" : qUnion([Q0])});
            skLineSegment(sketch, "E51", {"start": v(546.1, 1428.43) * mm, "end": v(917.57, 1371.6) * mm});
            skLineSegment(sketch, "E52", {"start": v(917.57, 1371.6) * mm, "end": v(918.54, 1377.88) * mm});
            skLineSegment(sketch, "E53", {"start": v(918.54, 1377.88) * mm, "end": v(546.1, 1434.86) * mm});
            skLineSegment(sketch, "E54", {"start": v(546.1, 1434.86) * mm, "end": v(546.1, 1428.43) * mm});
            skLineSegment(sketch, "E55", {"start": v(546.1, 1428.43) * mm, "end": v(241.3, 1371.6) * mm});
            skLineSegment(sketch, "E56", {"start": v(241.3, 1371.6) * mm, "end": v(240.14, 1377.84) * mm});
            skLineSegment(sketch, "E57", {"start": v(240.14, 1377.84) * mm, "end": v(546.1, 1434.86) * mm});
            skSolve(sketch);
        }
        {
            var Q0;
            {var subQ0=sQuery(id+"F35.wireOp",EDGE,"E52");Q0=makeQuery(id+"F35.imprint","IMPRINT",FACE,{"disambiguationData":[TD([[makeQuery(id+"F35.imprint","IMPRINT",EDGE,{"derivedFrom":subQ0}),1.0]])]});}
            extrude(context, id + "F36", {"entities" : qUnion([Q0]), "depth" : 25.4 * mm, "offsetDistance" : 25.4 * mm, "hasSecondDirection" : true, "secondDirectionOppositeDirection" : true, "secondDirectionDepth" : 1708.15 * mm});
        }
        {
            var Q0;
            Q0=makeQuery(id+"F35.imprint","IMPRINT",FACE,{"disambiguationData":[TD([[makeQuery(id+"F35.imprint","IMPRINT",EDGE,{"derivedFrom":sQuery(id+"F35.wireOp",EDGE,"E54")}),-1.0]])]});
            extrude(context, id + "F37", {"entities" : qUnion([Q0]), "depth" : 25.4 * mm, "offsetDistance" : 25.4 * mm, "hasSecondDirection" : true, "secondDirectionOppositeDirection" : true, "secondDirectionDepth" : 1708.15 * mm});
        }
        {
            var Q0;
            Q0=makeQuery(id+"F26.opExtrude","CAP_FACE",FACE,{"disambiguationData":[OSD([sQuery(id+"F25.wireOp",EDGE,"E37.bottom"),sQuery(id+"F25.wireOp",EDGE,"E37.top"),sQuery(id+"F25.wireOp",EDGE,"E37.left"),sQuery(id+"F25.wireOp",EDGE,"E37.right"),sQuery(id+"F25.wireOp",EDGE,"E39.bottom"),sQuery(id+"F25.wireOp",EDGE,"E40.bottom")])],"isStart":false});
            var sketch = newSketch(context, id + "F38", { "sketchPlane" : qUnion([Q0])});
            skLineSegment(sketch, "E58.bottom", {"start": v(-932.54, 565.14) * mm, "end": v(762, 565.14) * mm});
            skLineSegment(sketch, "E58.top", {"start": v(-932.54, 1378.17) * mm, "end": v(762, 1378.17) * mm});
            skLineSegment(sketch, "E58.left", {"start": v(-932.54, 565.14) * mm, "end": v(-932.54, 1378.17) * mm});
            skLineSegment(sketch, "E58.right", {"start": v(762, 565.14) * mm, "end": v(762, 1378.17) * mm});
            skLineSegment(sketch, "E59.bottom", {"start": v(762, 1378.17) * mm, "end": v(762, 1378.17) * mm});
            skLineSegment(sketch, "E59.top", {"start": v(762, 1378.56) * mm, "end": v(762, 1378.56) * mm});
            skLineSegment(sketch, "E59.left", {"start": v(762, 1378.56) * mm, "end": v(762, 1378.17) * mm});
            skLineSegment(sketch, "E59.right", {"start": v(762, 1378.56) * mm, "end": v(762, 1378.17) * mm});
            skSolve(sketch);
        }
        {
            var Q0;
            {var subQ0=sQuery(id+"F38.wireOp",EDGE,"E58.top");Q0=makeQuery(id+"F38.imprint","IMPRINT",FACE,{"disambiguationData":[TD([[makeQuery(id+"F38.imprint","IMPRINT",EDGE,{"derivedFrom":subQ0}),-1.0]])]});}
            var Q1;
            {var subQ3=makeQuery(id+"F26.opExtrude","CAP_EDGE",EDGE,{"disambiguationData":[OSD([sQuery(id+"F25.wireOp",EDGE,"E37.bottom")])],"isStart":false});var subQ5=sQuery(id+"F38.wireOp",EDGE,"E58.right");var subQ6=makeQuery(id+"F38.imprint","INTERSECT",VERTEX,{"derivedFrom":[subQ3,subQ5]});Q1=makeQuery(id+"F38.imprint","IMPRINT",FACE,{"disambiguationData":[TD([[makeQuery(id+"F38.imprint","IMPRINT",EDGE,{"disambiguationData":[TD([[subQ6,1.0]])],"derivedFrom":subQ3}),-1.0]])]});}
            var Q2;
            {var subQ0=sQuery(id+"F38.wireOp",EDGE,"E58.bottom");Q2=makeQuery(id+"F38.imprint","IMPRINT",FACE,{"disambiguationData":[TD([[makeQuery(id+"F38.imprint","IMPRINT",EDGE,{"derivedFrom":subQ0}),1.0]])]});}
            extrude(context, id + "F39", {"entities" : qUnion([Q0, Q1, Q2]), "depth" : 6.35 * mm, "offsetDistance" : 25.4 * mm});
        }
        {
            var Q0;
            Q0=makeQuery(id+"F29.opExtrude","CAP_FACE",FACE,{"disambiguationData":[OSD([sQuery(id+"F28.wireOp",EDGE,"E41.bottom"),sQuery(id+"F28.wireOp",EDGE,"E41.top"),sQuery(id+"F28.wireOp",EDGE,"E41.left"),sQuery(id+"F28.wireOp",EDGE,"E41.right")])],"isStart":false});
            var sketch = newSketch(context, id + "F40", { "sketchPlane" : qUnion([Q0])});
            skLineSegment(sketch, "E60.0", {"start": v(546.1, 1428.43) * mm, "end": v(879.47, 1377.43) * mm});
            skLineSegment(sketch, "E61.0", {"start": v(546.1, 1428.43) * mm, "end": v(285.75, 1379.89) * mm});
            skLineSegment(sketch, "E62.0", {"start": v(879.47, 565.14) * mm, "end": v(879.47, 1378.17) * mm});
            skLineSegment(sketch, "E63.0", {"start": v(854.07, 558.8) * mm, "end": v(301.62, 693.33) * mm});
            skLineSegment(sketch, "E64", {"start": v(301.62, 693.33) * mm, "end": v(285.75, 697.2) * mm});
            skLineSegment(sketch, "E65", {"start": v(879.47, 565.14) * mm, "end": v(879.47, 552.61) * mm});
            skLineSegment(sketch, "E66", {"start": v(854.07, 558.8) * mm, "end": v(879.47, 552.61) * mm});
            skPoint(sketch, "E67.orphan", {"position": v(917.57, 1371.6) * mm});
            skPoint(sketch, "E68.orphan", {"position": v(241.3, 1371.6) * mm});
            skLineSegment(sketch, "E69", {"start": v(279.4, 1378.7) * mm, "end": v(279.4, 698.74) * mm});
            skLineSegment(sketch, "E70", {"start": v(285.75, 1379.89) * mm, "end": v(279.4, 1378.7) * mm});
            skLineSegment(sketch, "E71", {"start": v(285.75, 697.2) * mm, "end": v(279.4, 698.74) * mm});
            skPoint(sketch, "E72.0.end.orphan", {"position": v(285.75, 800.1) * mm});
            skPoint(sketch, "E73.start.orphan", {"position": v(285.75, 1206.5) * mm});
            skSolve(sketch);
        }
        {
            var Q0;
            {var subQ1=sQuery(id+"F40.wireOp",EDGE,"E60.0");Q0=makeQuery(id+"F40.imprint","IMPRINT",FACE,{"disambiguationData":[TD([[makeQuery(id+"F40.imprint","IMPRINT",EDGE,{"derivedFrom":subQ1}),-1.0]])]});}
            var Q1;
            Q1=makeQuery(id+"F40.imprint","IMPRINT",FACE,{"disambiguationData":[TD([[makeQuery(id+"F40.imprint","IMPRINT",EDGE,{"derivedFrom":makeQuery(id+"F29.opExtrude","CAP_EDGE",EDGE,{"disambiguationData":[OSD([sQuery(id+"F28.wireOp",EDGE,"E41.bottom")])],"isStart":false})}),1.0]])]});
            extrude(context, id + "F41", {"entities" : qUnion([Q0, Q1]), "depth" : 6.35 * mm, "offsetDistance" : 25.4 * mm});
        }
        {
            var Q0;
            Q0=makeQuery(id+"F34.opExtrude","CAP_FACE",FACE,{"disambiguationData":[OSD([sQuery(id+"F33.wireOp",EDGE,"E50.bottom"),sQuery(id+"F33.wireOp",EDGE,"E50.top"),sQuery(id+"F33.wireOp",EDGE,"E50.left"),sQuery(id+"F33.wireOp",EDGE,"E50.right")])],"isStart":false});
            var sketch = newSketch(context, id + "F42", { "sketchPlane" : qUnion([Q0])});
            skLineSegment(sketch, "E74.bottom", {"start": v(935.73, 1380.34) * mm, "end": v(-762, 1380.34) * mm});
            skLineSegment(sketch, "E74.top", {"start": v(935.73, 710.2) * mm, "end": v(-762, 710.2) * mm});
            skLineSegment(sketch, "E74.left", {"start": v(935.73, 1380.34) * mm, "end": v(935.73, 710.2) * mm});
            skLineSegment(sketch, "E74.right", {"start": v(-762, 1380.34) * mm, "end": v(-762, 710.2) * mm});
            skSolve(sketch);
        }
        {
            var Q0;
            {var subQ2=sQuery(id+"F42.wireOp",EDGE,"E74.bottom");Q0=makeQuery(id+"F42.imprint","IMPRINT",FACE,{"disambiguationData":[TD([[makeQuery(id+"F42.imprint","IMPRINT",EDGE,{"derivedFrom":subQ2}),1.0]])]});}
            var Q1;
            {var subQ1=makeQuery(id+"F34.opExtrude","CAP_EDGE",EDGE,{"disambiguationData":[OSD([sQuery(id+"F33.wireOp",EDGE,"E50.bottom")])],"isStart":false});Q1=makeQuery(id+"F42.imprint","IMPRINT",FACE,{"disambiguationData":[TD([[makeQuery(id+"F42.imprint","IMPRINT",EDGE,{"derivedFrom":subQ1}),1.0]])]});}
            extrude(context, id + "F43", {"entities" : qUnion([Q0, Q1]), "depth" : 6.35 * mm, "offsetDistance" : 25.4 * mm});
        }
    });
